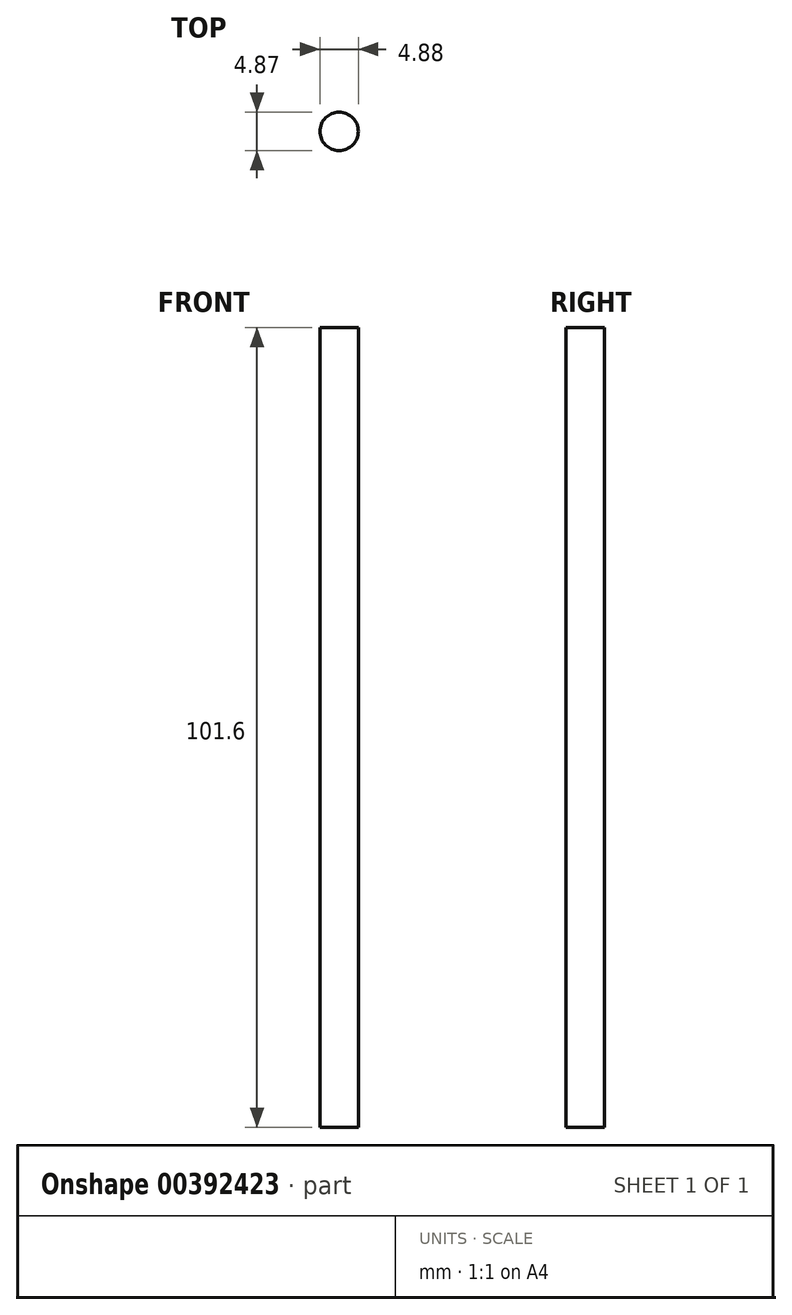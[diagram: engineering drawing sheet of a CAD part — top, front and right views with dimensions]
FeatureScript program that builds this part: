
annotation { "Feature Type Name" : "Feature", "Feature Type Description" : "" }
export const myFeature = defineFeature(function(context is Context, id is Id, definition is map)
    precondition{}
    {
        {
            var Q0;
            Q0=qCreatedBy(makeId("Top.planeOp"),FACE);
            var sketch = newSketch(context, id + "F0", { "sketchPlane" : qUnion([Q0])});
            skCircle(sketch, "E0", {"center": v(-16.86, 9.63) * mm, "radius": 2.44 * mm});
            skSolve(sketch);
        }
        {
            var Q0;
            Q0=makeQuery(id+"F0.imprint","IMPRINT",FACE,{"disambiguationData":[TD([[makeQuery(id+"F0.imprint","IMPRINT",EDGE,{"derivedFrom":sQuery(id+"F0.wireOp",EDGE,"E0")}),1.0]])]});
            extrude(context, id + "F1", {"entities" : qUnion([Q0]), "depth" : 101.6 * mm});
        }
    });
